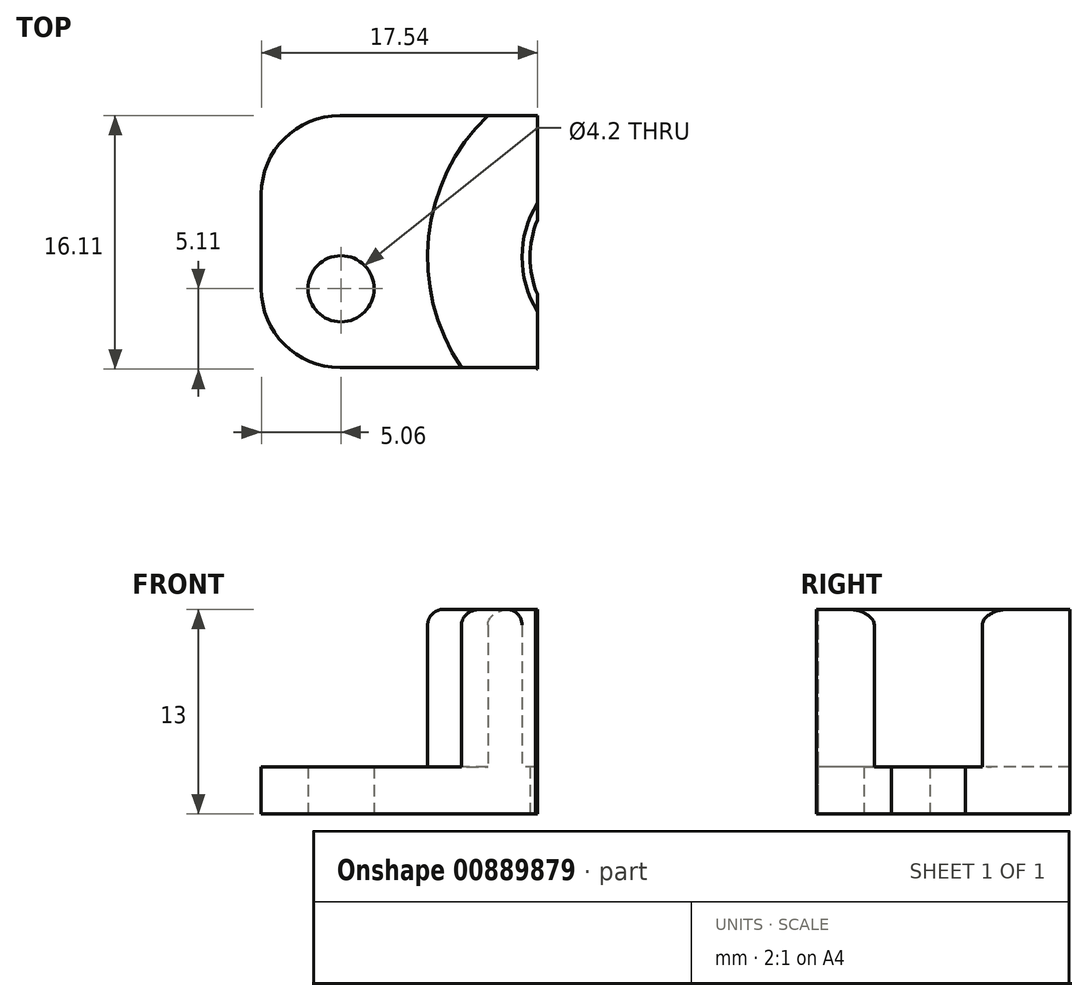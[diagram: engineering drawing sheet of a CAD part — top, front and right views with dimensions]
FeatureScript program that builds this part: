
annotation { "Feature Type Name" : "Feature", "Feature Type Description" : "" }
export const myFeature = defineFeature(function(context is Context, id is Id, definition is map)
    precondition{}
    {
        {
            var Q0;
            Q0=qCreatedBy(makeId("Top.planeOp"),FACE);
            var sketch = newSketch(context, id + "F0", { "sketchPlane" : qUnion([Q0])});
            skCircle(sketch, "E0", {"center": v(0, 0) * mm, "radius": 6 * mm});
            skCircle(sketch, "E1", {"center": v(0, 0) * mm, "radius": 9 * mm});
            skCircle(sketch, "E2", {"center": v(-18, -2) * mm, "radius": 2.1 * mm});
            skLineSegment(sketch, "E3.bottom", {"start": v(-23.06, -7) * mm, "end": v(0, -7) * mm});
            skLineSegment(sketch, "E3.top", {"start": v(-23.06, 9) * mm, "end": v(0, 9) * mm});
            skLineSegment(sketch, "E3.left", {"start": v(-23.06, -7) * mm, "end": v(-23.06, 9) * mm});
            skLineSegment(sketch, "E3.right", {"start": v(0, -7) * mm, "end": v(0, 9) * mm});
            skSolve(sketch);
        }
        {
            var Q0;
            Q0=makeQuery(id+"F0.imprint","IMPRINT",FACE,{"disambiguationData":[TD([[makeQuery(id+"F0.imprint","IMPRINT",EDGE,{"derivedFrom":sQuery(id+"F0.wireOp",EDGE,"E2")}),-1.0]])]});
            var Q1;
            {var subQ0=sQuery(id+"F0.wireOp",EDGE,"E3.right");var subQ3=sQuery(id+"F0.wireOp",EDGE,"E0");var subQ4=makeQuery(id+"F0.imprint","INTERSECT",VERTEX,{"disambiguationData":[OD(0.0)],"derivedFrom":[subQ3,subQ0]});Q1=makeQuery(id+"F0.imprint","IMPRINT",FACE,{"disambiguationData":[TD([[makeQuery(id+"F0.imprint","IMPRINT",EDGE,{"disambiguationData":[TD([[subQ4,1.0]])],"derivedFrom":subQ3}),-1.0]])]});}
            var Q2;
            {var subQ0=sQuery(id+"F0.wireOp",EDGE,"E3.right");var subQ3=sQuery(id+"F0.wireOp",EDGE,"E0");var subQ4=makeQuery(id+"F0.imprint","INTERSECT",VERTEX,{"disambiguationData":[OD(0.0)],"derivedFrom":[subQ3,subQ0]});Q2=makeQuery(id+"F0.imprint","IMPRINT",FACE,{"disambiguationData":[TD([[makeQuery(id+"F0.imprint","IMPRINT",EDGE,{"disambiguationData":[TD([[subQ4,-1.0]])],"derivedFrom":subQ3}),-1.0]])]});}
            extrude(context, id + "F1", {"entities" : qUnion([Q0, Q1, Q2]), "depth" : 3 * mm, "offsetDistance" : 25 * mm});
        }
        {
            var Q0;
            Q0=makeQuery(id+"F1.opExtrude","SWEPT_EDGE",EDGE,{"disambiguationData":[OSD([sQuery(id+"F0.wireOp",EDGE,"E3.top"),sQuery(id+"F0.wireOp",EDGE,"E3.left")])]});
            var Q1;
            Q1=makeQuery(id+"F1.opExtrude","SWEPT_EDGE",EDGE,{"disambiguationData":[OSD([sQuery(id+"F0.wireOp",EDGE,"E3.bottom"),sQuery(id+"F0.wireOp",EDGE,"E3.left")])]});
            fillet(context, id + "F2", {"entities" : qUnion([Q0, Q1]), "radius" : 5 * mm, "tangentPropagation" : true, "allowEdgeOverflow" : false});
        }
        {
            var Q0;
            Q0=makeQuery(id+"F1.opExtrude","CAP_FACE",FACE,{"disambiguationData":[OSD([sQuery(id+"F0.wireOp",EDGE,"E0"),sQuery(id+"F0.wireOp",EDGE,"E1"),sQuery(id+"F0.wireOp",EDGE,"E2"),sQuery(id+"F0.wireOp",EDGE,"E3.bottom"),sQuery(id+"F0.wireOp",EDGE,"E3.top"),sQuery(id+"F0.wireOp",EDGE,"E3.left")])],"isStart":false});
            var sketch = newSketch(context, id + "F3", { "sketchPlane" : qUnion([Q0])});
            skCircle(sketch, "E4", {"center": v(0, 0) * mm, "radius": 6.5 * mm});
            skCircle(sketch, "E5", {"center": v(0, 0) * mm, "radius": 12.5 * mm});
            skSolve(sketch);
        }
        {
            var Q0;
            Q0=makeQuery(id+"F3.imprint","IMPRINT",FACE,{"disambiguationData":[TD([[makeQuery(id+"F3.imprint","IMPRINT",EDGE,{"derivedFrom":sQuery(id+"F3.wireOp",EDGE,"E4")}),-1.0]])]});
            extrude(context, id + "F4", {"entities" : qUnion([Q0]), "operationType" : NewBodyOperationType.ADD, "depth" : 10 * mm, "offsetDistance" : 25 * mm});
        }
        {
            var Q0;
            Q0=makeQuery(id+"F4.opExtrude","CAP_EDGE",EDGE,{"disambiguationData":[OSD([sQuery(id+"F3.wireOp",EDGE,"E5")])],"isStart":false});
            var Q1;
            Q1=makeQuery(id+"F4.opExtrude","CAP_EDGE",EDGE,{"disambiguationData":[OSD([sQuery(id+"F3.wireOp",EDGE,"E4")])],"isStart":false});
            fillet(context, id + "F5", {"entities" : qUnion([Q0, Q1]), "radius" : 1 * mm, "tangentPropagation" : true, "allowEdgeOverflow" : false});
        }
        {
            var Q0;
            Q0=qCreatedBy(makeId("Top.planeOp"),FACE);
            var sketch = newSketch(context, id + "F6", { "sketchPlane" : qUnion([Q0])});
            skLineSegment(sketch, "E6.bottom", {"start": v(-5.52, 20.22) * mm, "end": v(12.42, 20.22) * mm});
            skLineSegment(sketch, "E6.top", {"start": v(-5.52, -16.26) * mm, "end": v(12.42, -16.26) * mm});
            skLineSegment(sketch, "E6.left", {"start": v(-5.52, 20.22) * mm, "end": v(-5.52, -16.26) * mm});
            skLineSegment(sketch, "E6.right", {"start": v(12.42, 20.22) * mm, "end": v(12.42, -16.26) * mm});
            skSolve(sketch);
        }
        {
            var Q0;
            Q0=makeQuery(id+"F6.imprint","IMPRINT",FACE,{"disambiguationData":[TD([[makeQuery(id+"F6.imprint","IMPRINT",EDGE,{"derivedFrom":sQuery(id+"F6.wireOp",EDGE,"E6.bottom")}),-1.0]])]});
            extrude(context, id + "F7", {"entities" : qUnion([Q0]), "operationType" : NewBodyOperationType.REMOVE, "endBound" : BoundingType.THROUGH_ALL, "depth" : 25 * mm, "offsetDistance" : 25 * mm});
        }
    });
